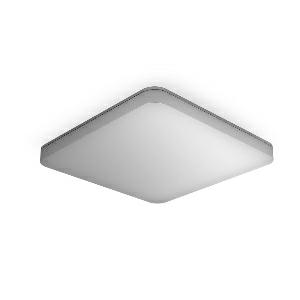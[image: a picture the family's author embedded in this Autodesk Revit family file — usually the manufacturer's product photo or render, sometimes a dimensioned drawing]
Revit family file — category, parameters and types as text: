
# Revit family: rs_pro_connect_r20_q_057183
name_source: partatom
category: Leuchten
revit_build: Autodesk Revit 2016 (Build: 20190508_0715(x64)
units: mm (PartAtom-declared; Revit-internal decimal feet)

## family parameters
Basisbauteil = Fläche
Beim Laden mit Abzugskörper schneiden = Nein
Bemaßung runder Anschluss = Durchmesser verwenden
Gemeinsam genutzt = Nein
Lichtquelle = Nein
Raumberechnungspunkt = Nein
Teiletyp = Normal

## types (1)
- RS PRO Connect R20 Q (1 x , 1900 lm, 3000 K)
    Beschreibung = Dimensions (L x W x H): 55 x 300 x 300 mm; Mains power supply: 220 – 240 V / 50 – 60 Hz; Sensor Technology: High frequency; Transmitter power: < 1 mW; HF-system: 5,8 GHz; Output: 16 W; Interconnection: Yes; Type of interconnection: Master/slave; Luminous flux: 1900 lm; Colour temperature: 3000 K; Colour variation LED: SDCM3; Colour Rendering Index CRI: 80-89; With lamp: Yes, STEINEL LED system; Lamp: LED cannot be replaced; LED life expectancy (max. °C): 50000 h; LED life expectancy (25 °C): 60000 h; Drop in luminous flux in accordance with LM80: L80B50; Base: without; LED cooling system: Passive Thermo Control; With motion detector: Yes; Detection: also through glass, wood and stud walls; Detection angle: 360 °; Angle of aperture: 160 °; Capability of masking out individual segments: Yes; Electronic scalability: Yes; Mechanical scalability: No; Reach, radial: Ø 10 m (79 m²); Reach, tangential: Ø 10 m (79 m²); Main light adjustable: 50 - 100 %; Continuous light: selectable; Photo-cell controller: Yes; Twilight setting: 2 – 2000 lx; Time setting: 5 sec – 30 min; Basic light level function: Yes; Basic light level function, detail: LED Backlight; Basic light level function time: 10-30 min, all night; Functions: Group parameterisation, Manual ON / ON-OFF, Master/slave override, Neighbouring-group function, Presence function, Backlight; Soft light start: Yes; Impact resistance: IK07; IP-rating: IP40; Protection class: II; Ambient temperature: -20 – 40 °C; Housing material: Plastic; Cover material: PC, opal; Manufacturer's Warranty: 5 years; Settings via: Bluetooth; With remote control: No; Version: warm white; PU1, EAN: 4007841057183
    CIE Flux Codes = 44 75 93 94 100
    Color Rendering = 80-89
    Color Temperature = 3000 K
    Frequency = 60 Hz, 50 Hz
    Height = 300 mm
    Hersteller = Steinel
    Lamp Light Flux = 1900 lm
    Lamp count = 1
    Lampe = 1 x
    Length = 55 mm
    Luminous efficacy = 0 lm/W
    ModVariant = Nein
    Modell = 057183
    Mounting Type = Surface mounted
    Number of Poles = 1
    OnlyDefault = Ja
    Power Factor = 1
    Product Name = RS PRO Connect R20 Q
    Product group = Sensor-switched indoor light
    ProductGroupID = 30
    Protection Class = Protection class II
    Protection Degree = IP 40
    RlxData = <blob elided: 174997 chars, md5=dc899e28>
    Scheinlast = 0 VA
    Socket = socket
    Standby Power = 0 W
    System Light Flux = 0 lm
    System Power = 0 W
    Typenbild = produkt1_057183.jpg
    Typenkommentare = Product without accessories
    URL = http://relux.com
    VarID = ---
    Voltage = 0 V
    Vorgabe-Ansicht = 1800 mm
    Weight = 0.00 kg
    Width = 300 mm

## geometry (parser evidence)
native form markers: Sweep x16
no freeform markers — native parametric forms only
